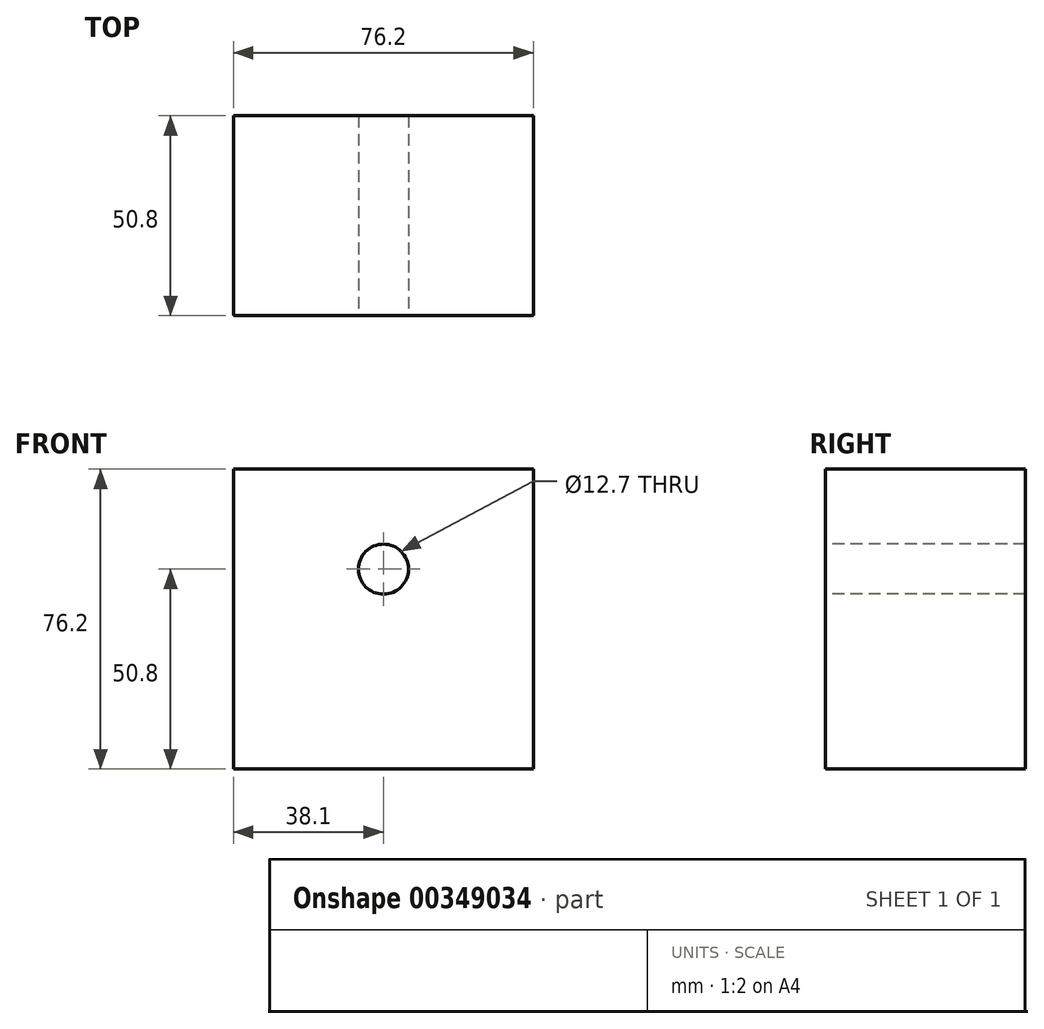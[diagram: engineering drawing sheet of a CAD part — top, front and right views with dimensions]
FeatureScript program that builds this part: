
annotation { "Feature Type Name" : "Feature", "Feature Type Description" : "" }
export const myFeature = defineFeature(function(context is Context, id is Id, definition is map)
    precondition{}
    {
        {
            var Q0;
            Q0=qCreatedBy(makeId("Front.planeOp"),FACE);
            var sketch = newSketch(context, id + "F0", { "sketchPlane" : qUnion([Q0])});
            skLineSegment(sketch, "E0.bottom", {"start": v(38.1, 38.1) * mm, "end": v(-38.1, 38.1) * mm});
            skLineSegment(sketch, "E0.top", {"start": v(38.1, -38.1) * mm, "end": v(-38.1, -38.1) * mm});
            skLineSegment(sketch, "E0.left", {"start": v(38.1, 38.1) * mm, "end": v(38.1, -38.1) * mm});
            skLineSegment(sketch, "E0.right", {"start": v(-38.1, 38.1) * mm, "end": v(-38.1, -38.1) * mm});
            skPoint(sketch, "E0.middle", {"position": v(0, 0) * mm});
            skSolve(sketch);
        }
        {
            var Q0;
            Q0=makeQuery(id+"F0.imprint","IMPRINT",FACE,{"disambiguationData":[TD([[makeQuery(id+"F0.imprint","IMPRINT",EDGE,{"derivedFrom":sQuery(id+"F0.wireOp",EDGE,"E0.bottom")}),1.0]])]});
            extrude(context, id + "F1", {"entities" : qUnion([Q0]), "endBound" : BoundingType.SYMMETRIC, "depth" : 50.8 * mm});
        }
        {
            var Q0;
            Q0=makeQuery(id+"F1.opExtrude","CAP_FACE",FACE,{"disambiguationData":[OSD([sQuery(id+"F0.wireOp",EDGE,"E0.bottom"),sQuery(id+"F0.wireOp",EDGE,"E0.top"),sQuery(id+"F0.wireOp",EDGE,"E0.left"),sQuery(id+"F0.wireOp",EDGE,"E0.right")])],"isStart":false});
            var sketch = newSketch(context, id + "F2", { "sketchPlane" : qUnion([Q0])});
            skCircle(sketch, "E1", {"center": v(0, 12.7) * mm, "radius": 6.35 * mm});
            skSolve(sketch);
        }
        {
            var Q0;
            Q0 = qSketchRegion(id + "F2", true);
            extrude(context, id + "F3", {"entities" : qUnion([Q0]), "operationType" : NewBodyOperationType.REMOVE, "endBound" : BoundingType.THROUGH_ALL, "oppositeDirection" : true, "depth" : 25.4 * mm});
        }
    });
